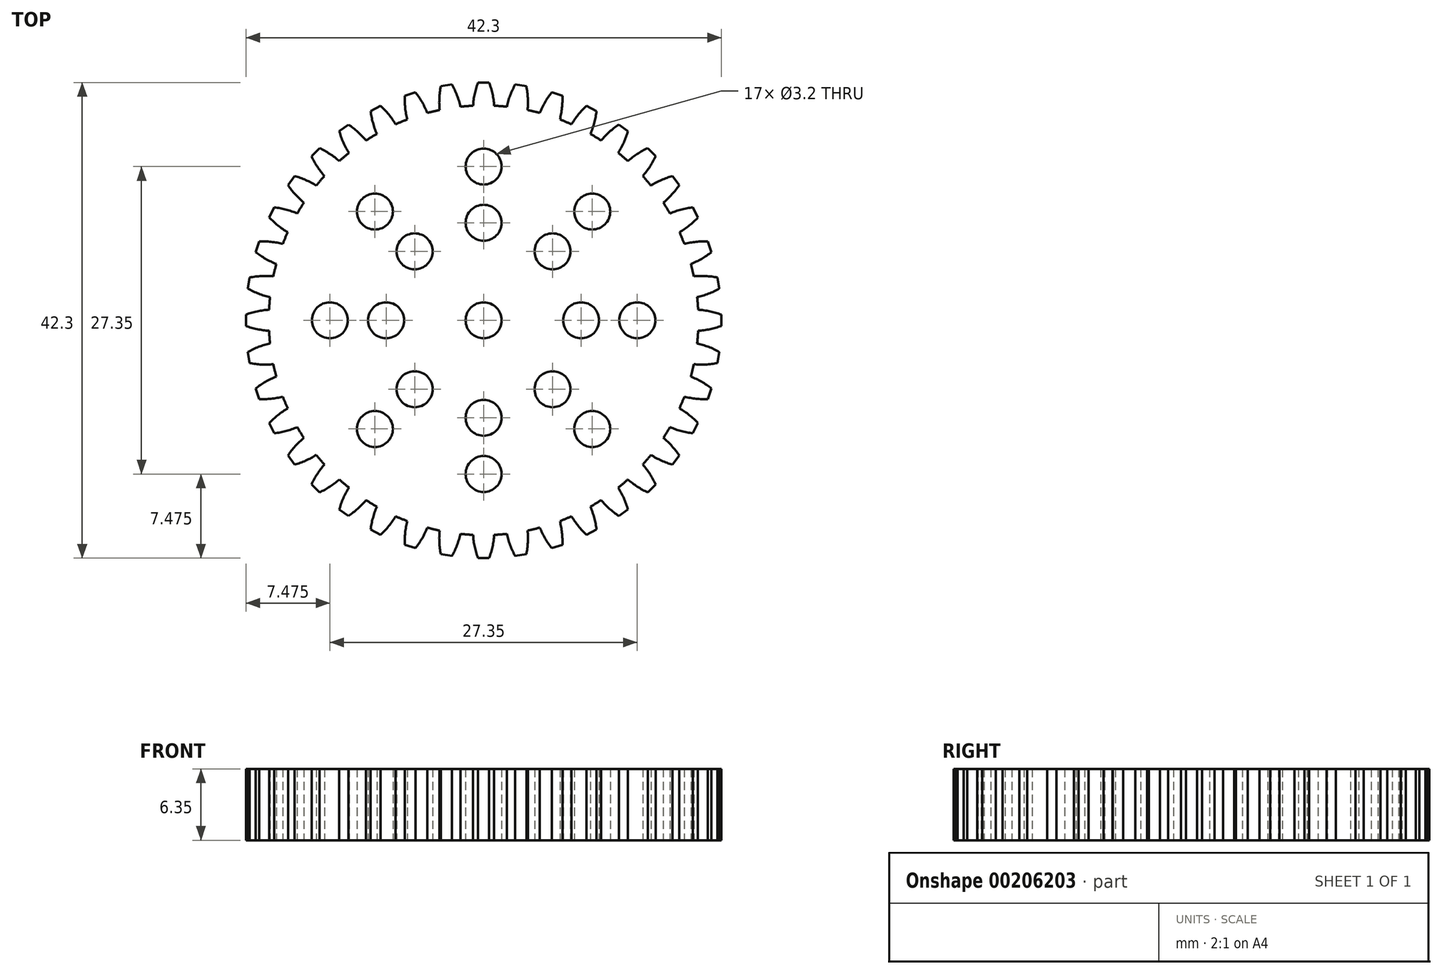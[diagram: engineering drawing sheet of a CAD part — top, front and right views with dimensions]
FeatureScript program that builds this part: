
annotation { "Feature Type Name" : "Feature", "Feature Type Description" : "" }
export const myFeature = defineFeature(function(context is Context, id is Id, definition is map)
    precondition{}
    {
        {
            var Q0;
            Q0=qCreatedBy(makeId("Top.planeOp"),FACE);
            var sketch = newSketch(context, id + "F0", { "sketchPlane" : qUnion([Q0])});
            skLineSegment(sketch, "E0", {"start": v(-0.5, 21.15) * mm, "end": v(0.5, 21.15) * mm});
            skArc(sketch, "E1", {"start": v(-0.5, 21.15) * mm, "mid": v(-0.8, 20.14) * mm, "end": v(-0.94, 19.09) * mm});
            skArc(sketch, "E2.MirrorCS", {"start": v(0.5, 21.15) * mm, "mid": v(0.8, 20.14) * mm, "end": v(0.94, 19.09) * mm});
            skCircle(sketch, "E3", {"center": v(0, 13.67) * mm, "radius": 1.6 * mm});
            skCircle(sketch, "E4", {"center": v(0, 8.67) * mm, "radius": 1.6 * mm});
            skLineSegment(sketch, "E5", {"start": v(0, 13.67) * mm, "end": v(0, 7.54) * mm});
            skCircle(sketch, "E6.1.0", {"center": v(-9.67, 9.67) * mm, "radius": 1.6 * mm});
            skCircle(sketch, "E6.1.1", {"center": v(-6.13, 6.13) * mm, "radius": 1.6 * mm});
            skCircle(sketch, "E6.2.0", {"center": v(-13.67, 0) * mm, "radius": 1.6 * mm});
            skCircle(sketch, "E6.2.1", {"center": v(-8.67, 0) * mm, "radius": 1.6 * mm});
            skCircle(sketch, "E6.3.0", {"center": v(-9.67, -9.67) * mm, "radius": 1.6 * mm});
            skCircle(sketch, "E6.3.1", {"center": v(-6.13, -6.13) * mm, "radius": 1.6 * mm});
            skCircle(sketch, "E6.4.0", {"center": v(0, -13.67) * mm, "radius": 1.6 * mm});
            skCircle(sketch, "E6.4.1", {"center": v(0, -8.67) * mm, "radius": 1.6 * mm});
            skCircle(sketch, "E6.5.0", {"center": v(9.67, -9.67) * mm, "radius": 1.6 * mm});
            skCircle(sketch, "E6.5.1", {"center": v(6.13, -6.13) * mm, "radius": 1.6 * mm});
            skCircle(sketch, "E6.6.0", {"center": v(13.67, 0) * mm, "radius": 1.6 * mm});
            skCircle(sketch, "E6.6.1", {"center": v(8.67, 0) * mm, "radius": 1.6 * mm});
            skCircle(sketch, "E6.7.0", {"center": v(9.67, 9.67) * mm, "radius": 1.6 * mm});
            skCircle(sketch, "E6.7.1", {"center": v(6.13, 6.13) * mm, "radius": 1.6 * mm});
            skArc(sketch, "E7", {"start": v(2.06, 19) * mm, "mid": v(1.5, 19.05) * mm, "end": v(0.94, 19.09) * mm});
            skArc(sketch, "E8.1.0", {"start": v(-2.81, 20.97) * mm, "mid": v(-2.36, 20.01) * mm, "end": v(-2.06, 19) * mm});
            skLineSegment(sketch, "E8.1.1", {"start": v(-3.8, 20.81) * mm, "end": v(-2.81, 20.97) * mm});
            skArc(sketch, "E8.1.2", {"start": v(-3.8, 20.81) * mm, "mid": v(-3.93, 19.76) * mm, "end": v(-3.91, 18.7) * mm});
            skArc(sketch, "E8.1.3", {"start": v(-0.94, 19.09) * mm, "mid": v(-1.5, 19.05) * mm, "end": v(-2.06, 19) * mm});
            skArc(sketch, "E8.2.0", {"start": v(-6.06, 20.27) * mm, "mid": v(-5.47, 19.4) * mm, "end": v(-5, 18.44) * mm});
            skLineSegment(sketch, "E8.2.1", {"start": v(-7.01, 19.96) * mm, "end": v(-6.06, 20.27) * mm});
            skArc(sketch, "E8.2.2", {"start": v(-7.01, 19.96) * mm, "mid": v(-6.98, 18.9) * mm, "end": v(-6.79, 17.86) * mm});
            skArc(sketch, "E8.2.3", {"start": v(-3.91, 18.7) * mm, "mid": v(-4.46, 18.58) * mm, "end": v(-5, 18.44) * mm});
            skArc(sketch, "E8.3.0", {"start": v(-9.16, 19.07) * mm, "mid": v(-8.43, 18.3) * mm, "end": v(-7.83, 17.43) * mm});
            skLineSegment(sketch, "E8.3.1", {"start": v(-10.05, 18.62) * mm, "end": v(-9.16, 19.07) * mm});
            skArc(sketch, "E8.3.2", {"start": v(-10.05, 18.62) * mm, "mid": v(-9.85, 17.58) * mm, "end": v(-9.5, 16.58) * mm});
            skArc(sketch, "E8.3.3", {"start": v(-6.79, 17.86) * mm, "mid": v(-7.31, 17.66) * mm, "end": v(-7.83, 17.43) * mm});
            skArc(sketch, "E8.4.0", {"start": v(-12.03, 17.4) * mm, "mid": v(-11.2, 16.76) * mm, "end": v(-10.46, 16) * mm});
            skLineSegment(sketch, "E8.4.1", {"start": v(-12.84, 16.82) * mm, "end": v(-12.03, 17.4) * mm});
            skArc(sketch, "E8.4.2", {"start": v(-12.84, 16.82) * mm, "mid": v(-12.48, 15.82) * mm, "end": v(-11.98, 14.9) * mm});
            skArc(sketch, "E8.4.3", {"start": v(-9.5, 16.58) * mm, "mid": v(-9.98, 16.3) * mm, "end": v(-10.46, 16) * mm});
            skArc(sketch, "E8.5.0", {"start": v(-14.6, 15.3) * mm, "mid": v(-13.68, 14.8) * mm, "end": v(-12.83, 14.16) * mm});
            skLineSegment(sketch, "E8.5.1", {"start": v(-15.3, 14.6) * mm, "end": v(-14.6, 15.3) * mm});
            skArc(sketch, "E8.5.2", {"start": v(-15.3, 14.6) * mm, "mid": v(-14.8, 13.68) * mm, "end": v(-14.16, 12.83) * mm});
            skArc(sketch, "E8.5.3", {"start": v(-11.98, 14.9) * mm, "mid": v(-12.41, 14.53) * mm, "end": v(-12.83, 14.16) * mm});
            skArc(sketch, "E8.6.0", {"start": v(-16.82, 12.84) * mm, "mid": v(-15.82, 12.48) * mm, "end": v(-14.9, 11.98) * mm});
            skLineSegment(sketch, "E8.6.1", {"start": v(-17.4, 12.03) * mm, "end": v(-16.82, 12.84) * mm});
            skArc(sketch, "E8.6.2", {"start": v(-17.4, 12.03) * mm, "mid": v(-16.76, 11.2) * mm, "end": v(-16, 10.46) * mm});
            skArc(sketch, "E8.6.3", {"start": v(-14.16, 12.83) * mm, "mid": v(-14.53, 12.41) * mm, "end": v(-14.9, 11.98) * mm});
            skArc(sketch, "E8.7.0", {"start": v(-18.62, 10.05) * mm, "mid": v(-17.58, 9.85) * mm, "end": v(-16.58, 9.5) * mm});
            skLineSegment(sketch, "E8.7.1", {"start": v(-19.07, 9.16) * mm, "end": v(-18.62, 10.05) * mm});
            skArc(sketch, "E8.7.2", {"start": v(-19.07, 9.16) * mm, "mid": v(-18.3, 8.43) * mm, "end": v(-17.43, 7.83) * mm});
            skArc(sketch, "E8.7.3", {"start": v(-16, 10.46) * mm, "mid": v(-16.3, 9.98) * mm, "end": v(-16.58, 9.5) * mm});
            skArc(sketch, "E8.8.0", {"start": v(-19.96, 7.01) * mm, "mid": v(-18.9, 6.98) * mm, "end": v(-17.86, 6.79) * mm});
            skLineSegment(sketch, "E8.8.1", {"start": v(-20.27, 6.06) * mm, "end": v(-19.96, 7.01) * mm});
            skArc(sketch, "E8.8.2", {"start": v(-20.27, 6.06) * mm, "mid": v(-19.4, 5.47) * mm, "end": v(-18.44, 5) * mm});
            skArc(sketch, "E8.8.3", {"start": v(-17.43, 7.83) * mm, "mid": v(-17.66, 7.31) * mm, "end": v(-17.86, 6.79) * mm});
            skArc(sketch, "E8.9.0", {"start": v(-20.81, 3.8) * mm, "mid": v(-19.76, 3.93) * mm, "end": v(-18.7, 3.91) * mm});
            skLineSegment(sketch, "E8.9.1", {"start": v(-20.97, 2.81) * mm, "end": v(-20.81, 3.8) * mm});
            skArc(sketch, "E8.9.2", {"start": v(-20.97, 2.81) * mm, "mid": v(-20.01, 2.36) * mm, "end": v(-19, 2.06) * mm});
            skArc(sketch, "E8.9.3", {"start": v(-18.44, 5) * mm, "mid": v(-18.58, 4.46) * mm, "end": v(-18.7, 3.91) * mm});
            skArc(sketch, "E8.10.0", {"start": v(-21.15, 0.5) * mm, "mid": v(-20.14, 0.8) * mm, "end": v(-19.09, 0.94) * mm});
            skLineSegment(sketch, "E8.10.1", {"start": v(-21.15, -0.5) * mm, "end": v(-21.15, 0.5) * mm});
            skArc(sketch, "E8.10.2", {"start": v(-21.15, -0.5) * mm, "mid": v(-20.14, -0.8) * mm, "end": v(-19.09, -0.94) * mm});
            skArc(sketch, "E8.10.3", {"start": v(-19, 2.06) * mm, "mid": v(-19.05, 1.5) * mm, "end": v(-19.09, 0.94) * mm});
            skArc(sketch, "E8.11.0", {"start": v(-20.97, -2.81) * mm, "mid": v(-20.01, -2.36) * mm, "end": v(-19, -2.06) * mm});
            skLineSegment(sketch, "E8.11.1", {"start": v(-20.81, -3.8) * mm, "end": v(-20.97, -2.81) * mm});
            skArc(sketch, "E8.11.2", {"start": v(-20.81, -3.8) * mm, "mid": v(-19.76, -3.93) * mm, "end": v(-18.7, -3.91) * mm});
            skArc(sketch, "E8.11.3", {"start": v(-19.09, -0.94) * mm, "mid": v(-19.05, -1.5) * mm, "end": v(-19, -2.06) * mm});
            skArc(sketch, "E8.12.0", {"start": v(-20.27, -6.06) * mm, "mid": v(-19.4, -5.47) * mm, "end": v(-18.44, -5) * mm});
            skLineSegment(sketch, "E8.12.1", {"start": v(-19.96, -7.01) * mm, "end": v(-20.27, -6.06) * mm});
            skArc(sketch, "E8.12.2", {"start": v(-19.96, -7.01) * mm, "mid": v(-18.9, -6.98) * mm, "end": v(-17.86, -6.79) * mm});
            skArc(sketch, "E8.12.3", {"start": v(-18.7, -3.91) * mm, "mid": v(-18.58, -4.46) * mm, "end": v(-18.44, -5) * mm});
            skArc(sketch, "E8.13.0", {"start": v(-19.07, -9.16) * mm, "mid": v(-18.3, -8.43) * mm, "end": v(-17.43, -7.83) * mm});
            skLineSegment(sketch, "E8.13.1", {"start": v(-18.62, -10.05) * mm, "end": v(-19.07, -9.16) * mm});
            skArc(sketch, "E8.13.2", {"start": v(-18.62, -10.05) * mm, "mid": v(-17.58, -9.85) * mm, "end": v(-16.58, -9.5) * mm});
            skArc(sketch, "E8.13.3", {"start": v(-17.86, -6.79) * mm, "mid": v(-17.66, -7.31) * mm, "end": v(-17.43, -7.83) * mm});
            skArc(sketch, "E8.14.0", {"start": v(-17.4, -12.03) * mm, "mid": v(-16.76, -11.2) * mm, "end": v(-16, -10.46) * mm});
            skLineSegment(sketch, "E8.14.1", {"start": v(-16.82, -12.84) * mm, "end": v(-17.4, -12.03) * mm});
            skArc(sketch, "E8.14.2", {"start": v(-16.82, -12.84) * mm, "mid": v(-15.82, -12.48) * mm, "end": v(-14.9, -11.98) * mm});
            skArc(sketch, "E8.14.3", {"start": v(-16.58, -9.5) * mm, "mid": v(-16.3, -9.98) * mm, "end": v(-16, -10.46) * mm});
            skArc(sketch, "E8.15.0", {"start": v(-15.3, -14.6) * mm, "mid": v(-14.8, -13.68) * mm, "end": v(-14.16, -12.83) * mm});
            skLineSegment(sketch, "E8.15.1", {"start": v(-14.6, -15.3) * mm, "end": v(-15.3, -14.6) * mm});
            skArc(sketch, "E8.15.2", {"start": v(-14.6, -15.3) * mm, "mid": v(-13.68, -14.8) * mm, "end": v(-12.83, -14.16) * mm});
            skArc(sketch, "E8.15.3", {"start": v(-14.9, -11.98) * mm, "mid": v(-14.53, -12.41) * mm, "end": v(-14.16, -12.83) * mm});
            skArc(sketch, "E8.16.0", {"start": v(-12.84, -16.82) * mm, "mid": v(-12.48, -15.82) * mm, "end": v(-11.98, -14.9) * mm});
            skLineSegment(sketch, "E8.16.1", {"start": v(-12.03, -17.4) * mm, "end": v(-12.84, -16.82) * mm});
            skArc(sketch, "E8.16.2", {"start": v(-12.03, -17.4) * mm, "mid": v(-11.2, -16.76) * mm, "end": v(-10.46, -16) * mm});
            skArc(sketch, "E8.16.3", {"start": v(-12.83, -14.16) * mm, "mid": v(-12.41, -14.53) * mm, "end": v(-11.98, -14.9) * mm});
            skArc(sketch, "E8.17.0", {"start": v(-10.05, -18.62) * mm, "mid": v(-9.85, -17.58) * mm, "end": v(-9.5, -16.58) * mm});
            skLineSegment(sketch, "E8.17.1", {"start": v(-9.16, -19.07) * mm, "end": v(-10.05, -18.62) * mm});
            skArc(sketch, "E8.17.2", {"start": v(-9.16, -19.07) * mm, "mid": v(-8.43, -18.3) * mm, "end": v(-7.83, -17.43) * mm});
            skArc(sketch, "E8.17.3", {"start": v(-10.46, -16) * mm, "mid": v(-9.98, -16.3) * mm, "end": v(-9.5, -16.58) * mm});
            skArc(sketch, "E8.18.0", {"start": v(-7.01, -19.96) * mm, "mid": v(-6.98, -18.9) * mm, "end": v(-6.79, -17.86) * mm});
            skLineSegment(sketch, "E8.18.1", {"start": v(-6.06, -20.27) * mm, "end": v(-7.01, -19.96) * mm});
            skArc(sketch, "E8.18.2", {"start": v(-6.06, -20.27) * mm, "mid": v(-5.47, -19.4) * mm, "end": v(-5, -18.44) * mm});
            skArc(sketch, "E8.18.3", {"start": v(-7.83, -17.43) * mm, "mid": v(-7.31, -17.66) * mm, "end": v(-6.79, -17.86) * mm});
            skArc(sketch, "E8.19.0", {"start": v(-3.8, -20.81) * mm, "mid": v(-3.93, -19.76) * mm, "end": v(-3.91, -18.7) * mm});
            skLineSegment(sketch, "E8.19.1", {"start": v(-2.81, -20.97) * mm, "end": v(-3.8, -20.81) * mm});
            skArc(sketch, "E8.19.2", {"start": v(-2.81, -20.97) * mm, "mid": v(-2.36, -20.01) * mm, "end": v(-2.06, -19) * mm});
            skArc(sketch, "E8.19.3", {"start": v(-5, -18.44) * mm, "mid": v(-4.46, -18.58) * mm, "end": v(-3.91, -18.7) * mm});
            skArc(sketch, "E8.20.0", {"start": v(-0.5, -21.15) * mm, "mid": v(-0.8, -20.14) * mm, "end": v(-0.94, -19.09) * mm});
            skLineSegment(sketch, "E8.20.1", {"start": v(0.5, -21.15) * mm, "end": v(-0.5, -21.15) * mm});
            skArc(sketch, "E8.20.2", {"start": v(0.5, -21.15) * mm, "mid": v(0.8, -20.14) * mm, "end": v(0.94, -19.09) * mm});
            skArc(sketch, "E8.20.3", {"start": v(-2.06, -19) * mm, "mid": v(-1.5, -19.05) * mm, "end": v(-0.94, -19.09) * mm});
            skArc(sketch, "E8.21.0", {"start": v(2.81, -20.97) * mm, "mid": v(2.36, -20.01) * mm, "end": v(2.06, -19) * mm});
            skLineSegment(sketch, "E8.21.1", {"start": v(3.8, -20.81) * mm, "end": v(2.81, -20.97) * mm});
            skArc(sketch, "E8.21.2", {"start": v(3.8, -20.81) * mm, "mid": v(3.93, -19.76) * mm, "end": v(3.91, -18.7) * mm});
            skArc(sketch, "E8.21.3", {"start": v(0.94, -19.09) * mm, "mid": v(1.5, -19.05) * mm, "end": v(2.06, -19) * mm});
            skArc(sketch, "E8.22.0", {"start": v(6.06, -20.27) * mm, "mid": v(5.47, -19.4) * mm, "end": v(5, -18.44) * mm});
            skLineSegment(sketch, "E8.22.1", {"start": v(7.01, -19.96) * mm, "end": v(6.06, -20.27) * mm});
            skArc(sketch, "E8.22.2", {"start": v(7.01, -19.96) * mm, "mid": v(6.98, -18.9) * mm, "end": v(6.79, -17.86) * mm});
            skArc(sketch, "E8.22.3", {"start": v(3.91, -18.7) * mm, "mid": v(4.46, -18.58) * mm, "end": v(5, -18.44) * mm});
            skArc(sketch, "E8.23.0", {"start": v(9.16, -19.07) * mm, "mid": v(8.43, -18.3) * mm, "end": v(7.83, -17.43) * mm});
            skLineSegment(sketch, "E8.23.1", {"start": v(10.05, -18.62) * mm, "end": v(9.16, -19.07) * mm});
            skArc(sketch, "E8.23.2", {"start": v(10.05, -18.62) * mm, "mid": v(9.85, -17.58) * mm, "end": v(9.5, -16.58) * mm});
            skArc(sketch, "E8.23.3", {"start": v(6.79, -17.86) * mm, "mid": v(7.31, -17.66) * mm, "end": v(7.83, -17.43) * mm});
            skArc(sketch, "E8.24.0", {"start": v(12.03, -17.4) * mm, "mid": v(11.2, -16.76) * mm, "end": v(10.46, -16) * mm});
            skLineSegment(sketch, "E8.24.1", {"start": v(12.84, -16.82) * mm, "end": v(12.03, -17.4) * mm});
            skArc(sketch, "E8.24.2", {"start": v(12.84, -16.82) * mm, "mid": v(12.48, -15.82) * mm, "end": v(11.98, -14.9) * mm});
            skArc(sketch, "E8.24.3", {"start": v(9.5, -16.58) * mm, "mid": v(9.98, -16.3) * mm, "end": v(10.46, -16) * mm});
            skArc(sketch, "E8.25.0", {"start": v(14.6, -15.3) * mm, "mid": v(13.68, -14.8) * mm, "end": v(12.83, -14.16) * mm});
            skLineSegment(sketch, "E8.25.1", {"start": v(15.3, -14.6) * mm, "end": v(14.6, -15.3) * mm});
            skArc(sketch, "E8.25.2", {"start": v(15.3, -14.6) * mm, "mid": v(14.8, -13.68) * mm, "end": v(14.16, -12.83) * mm});
            skArc(sketch, "E8.25.3", {"start": v(11.98, -14.9) * mm, "mid": v(12.41, -14.53) * mm, "end": v(12.83, -14.16) * mm});
            skArc(sketch, "E8.26.0", {"start": v(16.82, -12.84) * mm, "mid": v(15.82, -12.48) * mm, "end": v(14.9, -11.98) * mm});
            skLineSegment(sketch, "E8.26.1", {"start": v(17.4, -12.03) * mm, "end": v(16.82, -12.84) * mm});
            skArc(sketch, "E8.26.2", {"start": v(17.4, -12.03) * mm, "mid": v(16.76, -11.2) * mm, "end": v(16, -10.46) * mm});
            skArc(sketch, "E8.26.3", {"start": v(14.16, -12.83) * mm, "mid": v(14.53, -12.41) * mm, "end": v(14.9, -11.98) * mm});
            skArc(sketch, "E8.27.0", {"start": v(18.62, -10.05) * mm, "mid": v(17.58, -9.85) * mm, "end": v(16.58, -9.5) * mm});
            skLineSegment(sketch, "E8.27.1", {"start": v(19.07, -9.16) * mm, "end": v(18.62, -10.05) * mm});
            skArc(sketch, "E8.27.2", {"start": v(19.07, -9.16) * mm, "mid": v(18.3, -8.43) * mm, "end": v(17.43, -7.83) * mm});
            skArc(sketch, "E8.27.3", {"start": v(16, -10.46) * mm, "mid": v(16.3, -9.98) * mm, "end": v(16.58, -9.5) * mm});
            skArc(sketch, "E8.28.0", {"start": v(19.96, -7.01) * mm, "mid": v(18.9, -6.98) * mm, "end": v(17.86, -6.79) * mm});
            skLineSegment(sketch, "E8.28.1", {"start": v(20.27, -6.06) * mm, "end": v(19.96, -7.01) * mm});
            skArc(sketch, "E8.28.2", {"start": v(20.27, -6.06) * mm, "mid": v(19.4, -5.47) * mm, "end": v(18.44, -5) * mm});
            skArc(sketch, "E8.28.3", {"start": v(17.43, -7.83) * mm, "mid": v(17.66, -7.31) * mm, "end": v(17.86, -6.79) * mm});
            skArc(sketch, "E8.29.0", {"start": v(20.81, -3.8) * mm, "mid": v(19.76, -3.93) * mm, "end": v(18.7, -3.91) * mm});
            skLineSegment(sketch, "E8.29.1", {"start": v(20.97, -2.81) * mm, "end": v(20.81, -3.8) * mm});
            skArc(sketch, "E8.29.2", {"start": v(20.97, -2.81) * mm, "mid": v(20.01, -2.36) * mm, "end": v(19, -2.06) * mm});
            skArc(sketch, "E8.29.3", {"start": v(18.44, -5) * mm, "mid": v(18.58, -4.46) * mm, "end": v(18.7, -3.91) * mm});
            skArc(sketch, "E8.30.0", {"start": v(21.15, -0.5) * mm, "mid": v(20.14, -0.8) * mm, "end": v(19.09, -0.94) * mm});
            skLineSegment(sketch, "E8.30.1", {"start": v(21.15, 0.5) * mm, "end": v(21.15, -0.5) * mm});
            skArc(sketch, "E8.30.2", {"start": v(21.15, 0.5) * mm, "mid": v(20.14, 0.8) * mm, "end": v(19.09, 0.94) * mm});
            skArc(sketch, "E8.30.3", {"start": v(19, -2.06) * mm, "mid": v(19.05, -1.5) * mm, "end": v(19.09, -0.94) * mm});
            skArc(sketch, "E8.31.0", {"start": v(20.97, 2.81) * mm, "mid": v(20.01, 2.36) * mm, "end": v(19, 2.06) * mm});
            skLineSegment(sketch, "E8.31.1", {"start": v(20.81, 3.8) * mm, "end": v(20.97, 2.81) * mm});
            skArc(sketch, "E8.31.2", {"start": v(20.81, 3.8) * mm, "mid": v(19.76, 3.93) * mm, "end": v(18.7, 3.91) * mm});
            skArc(sketch, "E8.31.3", {"start": v(19.09, 0.94) * mm, "mid": v(19.05, 1.5) * mm, "end": v(19, 2.06) * mm});
            skArc(sketch, "E8.32.0", {"start": v(20.27, 6.06) * mm, "mid": v(19.4, 5.47) * mm, "end": v(18.44, 5) * mm});
            skLineSegment(sketch, "E8.32.1", {"start": v(19.96, 7.01) * mm, "end": v(20.27, 6.06) * mm});
            skArc(sketch, "E8.32.2", {"start": v(19.96, 7.01) * mm, "mid": v(18.9, 6.98) * mm, "end": v(17.86, 6.79) * mm});
            skArc(sketch, "E8.32.3", {"start": v(18.7, 3.91) * mm, "mid": v(18.58, 4.46) * mm, "end": v(18.44, 5) * mm});
            skArc(sketch, "E8.33.0", {"start": v(19.07, 9.16) * mm, "mid": v(18.3, 8.43) * mm, "end": v(17.43, 7.83) * mm});
            skLineSegment(sketch, "E8.33.1", {"start": v(18.62, 10.05) * mm, "end": v(19.07, 9.16) * mm});
            skArc(sketch, "E8.33.2", {"start": v(18.62, 10.05) * mm, "mid": v(17.58, 9.85) * mm, "end": v(16.58, 9.5) * mm});
            skArc(sketch, "E8.33.3", {"start": v(17.86, 6.79) * mm, "mid": v(17.66, 7.31) * mm, "end": v(17.43, 7.83) * mm});
            skArc(sketch, "E8.34.0", {"start": v(17.4, 12.03) * mm, "mid": v(16.76, 11.2) * mm, "end": v(16, 10.46) * mm});
            skLineSegment(sketch, "E8.34.1", {"start": v(16.82, 12.84) * mm, "end": v(17.4, 12.03) * mm});
            skArc(sketch, "E8.34.2", {"start": v(16.82, 12.84) * mm, "mid": v(15.82, 12.48) * mm, "end": v(14.9, 11.98) * mm});
            skArc(sketch, "E8.34.3", {"start": v(16.58, 9.5) * mm, "mid": v(16.3, 9.98) * mm, "end": v(16, 10.46) * mm});
            skArc(sketch, "E8.35.0", {"start": v(15.3, 14.6) * mm, "mid": v(14.8, 13.68) * mm, "end": v(14.16, 12.83) * mm});
            skLineSegment(sketch, "E8.35.1", {"start": v(14.6, 15.3) * mm, "end": v(15.3, 14.6) * mm});
            skArc(sketch, "E8.35.2", {"start": v(14.6, 15.3) * mm, "mid": v(13.68, 14.8) * mm, "end": v(12.83, 14.16) * mm});
            skArc(sketch, "E8.35.3", {"start": v(14.9, 11.98) * mm, "mid": v(14.53, 12.41) * mm, "end": v(14.16, 12.83) * mm});
            skArc(sketch, "E8.36.0", {"start": v(12.84, 16.82) * mm, "mid": v(12.48, 15.82) * mm, "end": v(11.98, 14.9) * mm});
            skLineSegment(sketch, "E8.36.1", {"start": v(12.03, 17.4) * mm, "end": v(12.84, 16.82) * mm});
            skArc(sketch, "E8.36.2", {"start": v(12.03, 17.4) * mm, "mid": v(11.2, 16.76) * mm, "end": v(10.46, 16) * mm});
            skArc(sketch, "E8.36.3", {"start": v(12.83, 14.16) * mm, "mid": v(12.41, 14.53) * mm, "end": v(11.98, 14.9) * mm});
            skArc(sketch, "E8.37.0", {"start": v(10.05, 18.62) * mm, "mid": v(9.85, 17.58) * mm, "end": v(9.5, 16.58) * mm});
            skLineSegment(sketch, "E8.37.1", {"start": v(9.16, 19.07) * mm, "end": v(10.05, 18.62) * mm});
            skArc(sketch, "E8.37.2", {"start": v(9.16, 19.07) * mm, "mid": v(8.43, 18.3) * mm, "end": v(7.83, 17.43) * mm});
            skArc(sketch, "E8.37.3", {"start": v(10.46, 16) * mm, "mid": v(9.98, 16.3) * mm, "end": v(9.5, 16.58) * mm});
            skArc(sketch, "E8.38.0", {"start": v(7.01, 19.96) * mm, "mid": v(6.98, 18.9) * mm, "end": v(6.79, 17.86) * mm});
            skLineSegment(sketch, "E8.38.1", {"start": v(6.06, 20.27) * mm, "end": v(7.01, 19.96) * mm});
            skArc(sketch, "E8.38.2", {"start": v(6.06, 20.27) * mm, "mid": v(5.47, 19.4) * mm, "end": v(5, 18.44) * mm});
            skArc(sketch, "E8.38.3", {"start": v(7.83, 17.43) * mm, "mid": v(7.31, 17.66) * mm, "end": v(6.79, 17.86) * mm});
            skArc(sketch, "E8.39.0", {"start": v(3.8, 20.81) * mm, "mid": v(3.93, 19.76) * mm, "end": v(3.91, 18.7) * mm});
            skLineSegment(sketch, "E8.39.1", {"start": v(2.81, 20.97) * mm, "end": v(3.8, 20.81) * mm});
            skArc(sketch, "E8.39.2", {"start": v(2.81, 20.97) * mm, "mid": v(2.36, 20.01) * mm, "end": v(2.06, 19) * mm});
            skArc(sketch, "E8.39.3", {"start": v(5, 18.44) * mm, "mid": v(4.46, 18.58) * mm, "end": v(3.91, 18.7) * mm});
            skCircle(sketch, "E9", {"center": v(0, 0) * mm, "radius": 1.6 * mm});
            skSolve(sketch);
        }
        {
            var Q0;
            Q0=makeQuery(id+"F0.imprint","IMPRINT",FACE,{"disambiguationData":[TD([[makeQuery(id+"F0.imprint","IMPRINT",EDGE,{"derivedFrom":sQuery(id+"F0.wireOp",EDGE,"E0")}),-1.0]])]});
            extrude(context, id + "F1", {"entities" : qUnion([Q0]), "depth" : 6.35 * mm});
        }
    });
